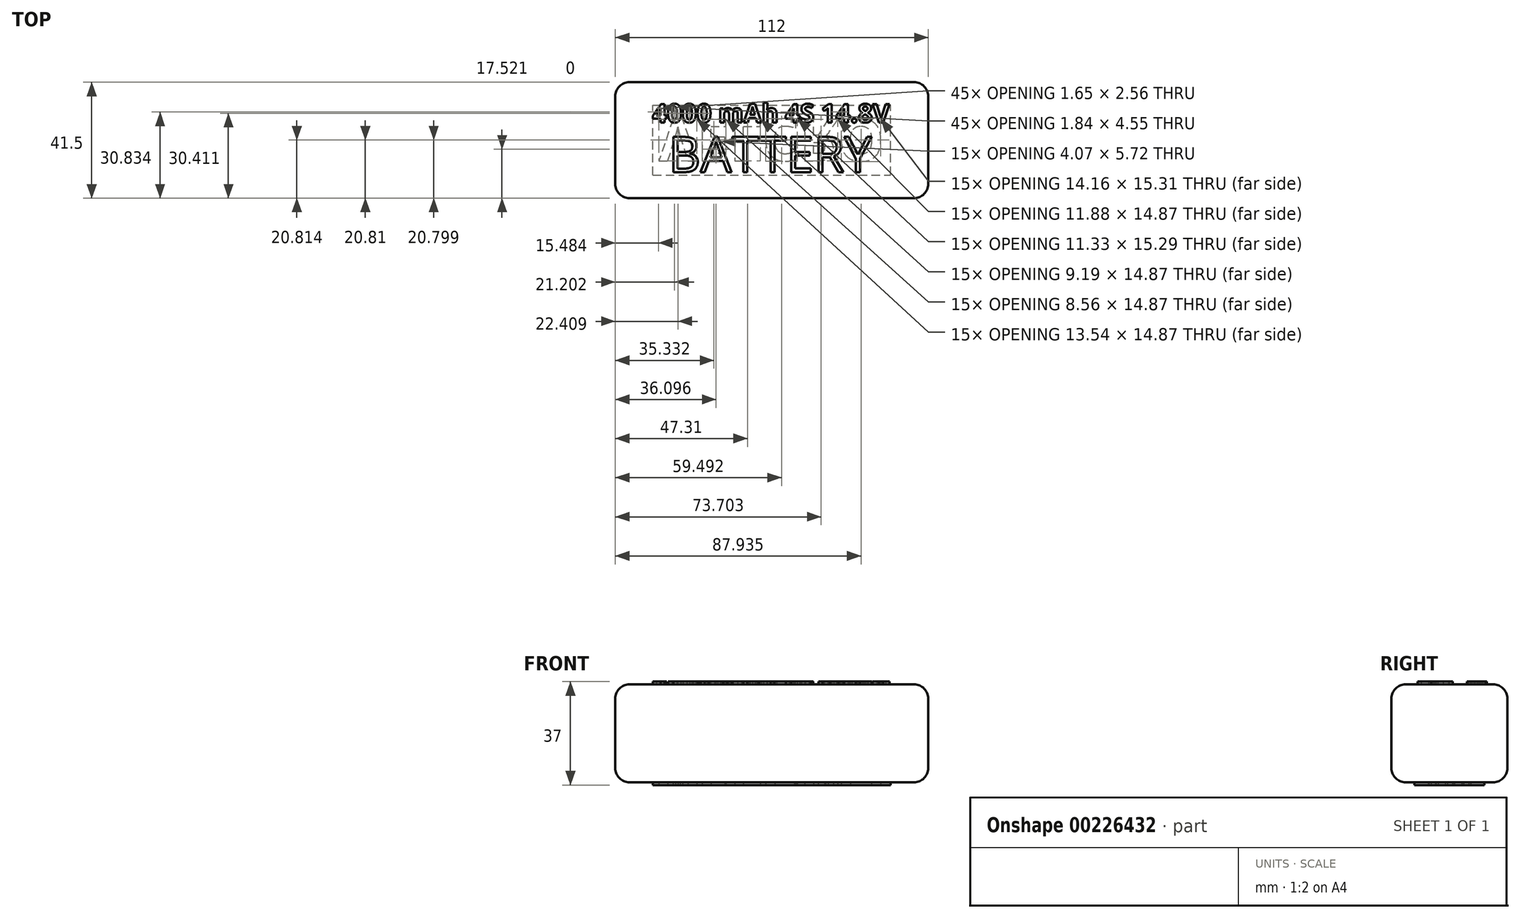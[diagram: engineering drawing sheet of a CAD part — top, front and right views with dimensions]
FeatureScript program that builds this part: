
annotation { "Feature Type Name" : "Feature", "Feature Type Description" : "" }
export const myFeature = defineFeature(function(context is Context, id is Id, definition is map)
    precondition{}
    {
        {
            var Q0;
            Q0=qCreatedBy(makeId("Front.planeOp"),FACE);
            var sketch = newSketch(context, id + "F0", { "sketchPlane" : qUnion([Q0])});
            skLineSegment(sketch, "E0.bottom", {"start": v(0, 0) * mm, "end": v(112, 0) * mm});
            skLineSegment(sketch, "E0.top", {"start": v(0, -35) * mm, "end": v(112, -35) * mm});
            skLineSegment(sketch, "E0.left", {"start": v(0, 0) * mm, "end": v(0, -35) * mm});
            skLineSegment(sketch, "E0.right", {"start": v(112, 0) * mm, "end": v(112, -35) * mm});
            skSolve(sketch);
        }
        {
            var Q0;
            Q0=makeQuery(id+"F0.imprint","IMPRINT",FACE,{"disambiguationData":[TD([[makeQuery(id+"F0.imprint","IMPRINT",EDGE,{"derivedFrom":sQuery(id+"F0.wireOp",EDGE,"E0.bottom")}),-1.0]])]});
            extrude(context, id + "F1", {"entities" : qUnion([Q0]), "depth" : 41.5 * mm, "offsetDistance" : 25.4 * mm});
        }
        {
            var Q0;
            Q0=makeQuery(id+"F1.opExtrude","SWEPT_FACE",FACE,{"disambiguationData":[OSD([sQuery(id+"F0.wireOp",EDGE,"E0.top")])]});
            var sketch = newSketch(context, id + "F2", { "sketchPlane" : qUnion([Q0])});
            skLineSegment(sketch, "E1.bottom", {"start": v(13.5, 33.25) * mm, "end": v(98.5, 33.25) * mm});
            skLineSegment(sketch, "E1.top", {"start": v(13.5, 8.25) * mm, "end": v(98.5, 8.25) * mm});
            skLineSegment(sketch, "E1.left", {"start": v(13.5, 33.25) * mm, "end": v(13.5, 8.25) * mm});
            skLineSegment(sketch, "E1.right", {"start": v(98.5, 33.25) * mm, "end": v(98.5, 8.25) * mm});
            skLineSegment(sketch, "E2", {"start": v(43.64, 33.25) * mm, "end": v(43.64, 41.5) * mm});
            skLineSegment(sketch, "E3", {"start": v(98.5, 17.56) * mm, "end": v(112, 17.56) * mm});
            skLineSegment(sketch, "E4", {"start": v(68.94, 8.25) * mm, "end": v(68.94, 0) * mm});
            skLineSegment(sketch, "E5", {"start": v(13.5, 17.8) * mm, "end": v(0, 17.8) * mm});
            skSolve(sketch);
        }
        {
            var Q0;
            {var subQ4=sQuery(id+"F2.wireOp",EDGE,"E1.left");var subQ6=sQuery(id+"F2.wireOp",EDGE,"E1.bottom");var subQ9=makeQuery(id+"F2.imprint","INTERSECT",VERTEX,{"derivedFrom":[subQ6,subQ4]});Q0=makeQuery(id+"F2.imprint","IMPRINT",FACE,{"disambiguationData":[TD([[makeQuery(id+"F2.imprint","IMPRINT",EDGE,{"disambiguationData":[TD([[subQ9,-1.0]])],"derivedFrom":subQ6}),-1.0]])]});}
            extrude(context, id + "F3", {"entities" : qUnion([Q0]), "depth" : 1 * mm, "offsetDistance" : 25.4 * mm});
        }
        {
            var Q0;
            Q0=makeQuery(id+"F1.opExtrude","SWEPT_FACE",FACE,{"disambiguationData":[OSD([sQuery(id+"F0.wireOp",EDGE,"E0.bottom")])]});
            var Q1;
            Q1=makeQuery(id+"F1.opExtrude","SWEPT_FACE",FACE,{"disambiguationData":[OSD([sQuery(id+"F0.wireOp",EDGE,"E0.right")])]});
            var Q2;
            Q2=makeQuery(id+"F1.opExtrude","CAP_FACE",FACE,{"disambiguationData":[OSD([sQuery(id+"F0.wireOp",EDGE,"E0.bottom"),sQuery(id+"F0.wireOp",EDGE,"E0.top"),sQuery(id+"F0.wireOp",EDGE,"E0.left"),sQuery(id+"F0.wireOp",EDGE,"E0.right")])],"isStart":false});
            var Q3;
            Q3=makeQuery(id+"F1.opExtrude","CAP_FACE",FACE,{"disambiguationData":[OSD([sQuery(id+"F0.wireOp",EDGE,"E0.bottom"),sQuery(id+"F0.wireOp",EDGE,"E0.top"),sQuery(id+"F0.wireOp",EDGE,"E0.left"),sQuery(id+"F0.wireOp",EDGE,"E0.right")])],"isStart":true});
            var Q4;
            Q4=makeQuery(id+"F1.opExtrude","SWEPT_FACE",FACE,{"disambiguationData":[OSD([sQuery(id+"F0.wireOp",EDGE,"E0.left")])]});
            fillet(context, id + "F4", {"entities" : qUnion([Q0, Q1, Q2, Q3, Q4]), "radius" : 5.08 * mm, "tangentPropagation" : true, "allowEdgeOverflow" : false});
        }
        {
            var Q0;
            Q0=makeQuery(id+"F1.opExtrude","SWEPT_FACE",FACE,{"disambiguationData":[OSD([sQuery(id+"F0.wireOp",EDGE,"E0.bottom")])]});
            var sketch = newSketch(context, id + "F5", { "sketchPlane" : qUnion([Q0])});
            skText(sketch, "E6", { "text": "4000 mAh 4S 14.8V", "fontName": "OpenSans-Bold.ttf"});
            skLineSegment(sketch, "E7", {"start": v(5.08, -10.72) * mm, "end": v(13.27, -10.72) * mm});
            skLineSegment(sketch, "E8", {"start": v(98.73, -11.07) * mm, "end": v(106.92, -11.07) * mm});
            skText(sketch, "E9", { "text": "BATTERY", "fontName": "OpenSans-Regular.ttf"});
            skLineSegment(sketch, "E10", {"start": v(19.08, -25.81) * mm, "end": v(5.08, -25.81) * mm});
            skLineSegment(sketch, "E11", {"start": v(92.92, -25.81) * mm, "end": v(106.92, -25.81) * mm});
            const initialGuessF5  = {"E6": [0.01327, -0.0144, 1, 0, 0.00667], "E9": [0.01908, -0.03216, 1, 0, 0.0127]};
            skSetInitialGuess(sketch, initialGuessF5);
            skSolve(sketch);
        }
        {
            var Q0;
            Q0 = qSketchRegion(id + "F5", true);
            extrude(context, id + "F6", {"entities" : qUnion([Q0]), "depth" : 1 * mm, "offsetDistance" : 25.4 * mm});
        }
        {
            var Q0;
            Q0=makeQuery(id+"F3.opExtrude","CAP_FACE",FACE,{"disambiguationData":[OSD([sQuery(id+"F2.wireOp",EDGE,"E1.bottom"),sQuery(id+"F2.wireOp",EDGE,"E1.top"),sQuery(id+"F2.wireOp",EDGE,"E1.left"),sQuery(id+"F2.wireOp",EDGE,"E1.right")])],"isStart":false});
            var sketch = newSketch(context, id + "F7", { "sketchPlane" : qUnion([Q0])});
            skText(sketch, "E12", { "text": "VELCRO", "fontName": "OpenSans-Bold.ttf"});
            skLineSegment(sketch, "E13", {"start": v(56, 28.25) * mm, "end": v(56, 33.25) * mm});
            skLineSegment(sketch, "E14", {"start": v(56, 13.25) * mm, "end": v(56, 8.25) * mm});
            skLineSegment(sketch, "E15", {"start": v(96.36, 20.75) * mm, "end": v(98.5, 20.75) * mm});
            skLineSegment(sketch, "E16", {"start": v(15.64, 20.75) * mm, "end": v(13.5, 20.75) * mm});
            const initialGuessF7  = {"E12": [0.01564, 0.01325, 1, 0, 0.015]};
            skSetInitialGuess(sketch, initialGuessF7);
            skSolve(sketch);
        }
        {
            var Q0;
            Q0 = qSketchRegion(id + "F7", true);
            extrude(context, id + "F8", {"entities" : qUnion([Q0]), "operationType" : NewBodyOperationType.REMOVE, "oppositeDirection" : true, "depth" : 1 * mm, "offsetDistance" : 25.4 * mm});
        }
        {
            var Q0;
            Q0=makeQuery(id+"F1.opExtrude","SWEPT_FACE",FACE,{"disambiguationData":[OSD([sQuery(id+"F0.wireOp",EDGE,"E0.top")])]});
            var sketch = newSketch(context, id + "F9", { "sketchPlane" : qUnion([Q0])});
            skLineSegment(sketch, "E17.0", {"start": v(56, 28.25) * mm, "end": v(56, 33.25) * mm});
            skLineSegment(sketch, "E17.1", {"start": v(56, 13.25) * mm, "end": v(56, 8.25) * mm});
            skLineSegment(sketch, "E17.2", {"start": v(96.36, 20.75) * mm, "end": v(98.5, 20.75) * mm});
            skLineSegment(sketch, "E17.3", {"start": v(15.64, 20.75) * mm, "end": v(13.5, 20.75) * mm});
            skLineSegment(sketch, "E18.0", {"start": v(15.64, 13.25) * mm, "end": v(15.64, 28.25) * mm, "construction": true});
            skLineSegment(sketch, "E19.0", {"start": v(15.64, 13.25) * mm, "end": v(96.36, 13.25) * mm, "construction": true});
            skLineSegment(sketch, "E20.0", {"start": v(15.64, 28.25) * mm, "end": v(96.36, 28.25) * mm, "construction": true});
            skLineSegment(sketch, "E21.0", {"start": v(96.36, 13.25) * mm, "end": v(96.36, 28.25) * mm, "construction": true});
            skLineSegment(sketch, "E22.0.0", {"start": v(98.5, 8.25) * mm, "end": v(98.5, 20.75) * mm});
            skLineSegment(sketch, "E22.0.1", {"start": v(98.5, 20.75) * mm, "end": v(98.5, 33.25) * mm});
            skLineSegment(sketch, "E22.0.2", {"start": v(98.5, 33.25) * mm, "end": v(56, 33.25) * mm});
            skLineSegment(sketch, "E22.0.3", {"start": v(56, 33.25) * mm, "end": v(13.5, 33.25) * mm});
            skLineSegment(sketch, "E22.0.4", {"start": v(13.5, 33.25) * mm, "end": v(13.5, 20.75) * mm});
            skLineSegment(sketch, "E22.0.5", {"start": v(13.5, 20.75) * mm, "end": v(13.5, 8.25) * mm});
            skLineSegment(sketch, "E22.0.6", {"start": v(13.5, 8.25) * mm, "end": v(56, 8.25) * mm});
            skLineSegment(sketch, "E22.0.7", {"start": v(56, 8.25) * mm, "end": v(98.5, 8.25) * mm});
            skText(sketch, "E23", { "text": "VELCRO\n", "fontName": "OpenSans-Bold.ttf"});
            const initialGuessF9  = {"E23": [0.01564, 0.01325, 1, 0, 0.015]};
            skSetInitialGuess(sketch, initialGuessF9);
            skSolve(sketch);
        }
        {
            var Q0;
            Q0=makeQuery(id+"F9.imprint","IMPRINT",FACE,{"disambiguationData":[TD([[makeQuery(id+"F9.imprint","IMPRINT",EDGE,{"derivedFrom":sQuery(id+"F9.wireOp",EDGE,"E23.sketch_text.stroke-0")}),-1.0]])]});
            var Q1;
            Q1=makeQuery(id+"F9.imprint","IMPRINT",FACE,{"disambiguationData":[TD([[makeQuery(id+"F9.imprint","IMPRINT",EDGE,{"derivedFrom":sQuery(id+"F9.wireOp",EDGE,"E23.sketch_text.stroke-10")}),-1.0]])]});
            var Q2;
            Q2=makeQuery(id+"F9.imprint","IMPRINT",FACE,{"disambiguationData":[TD([[makeQuery(id+"F9.imprint","IMPRINT",EDGE,{"derivedFrom":sQuery(id+"F9.wireOp",EDGE,"E23.sketch_text.stroke-22")}),-1.0]])]});
            var Q3;
            Q3=makeQuery(id+"F9.imprint","IMPRINT",FACE,{"disambiguationData":[TD([[makeQuery(id+"F9.imprint","IMPRINT",EDGE,{"derivedFrom":sQuery(id+"F9.wireOp",EDGE,"E23.sketch_text.stroke-28")}),-1.0]])]});
            var Q4;
            Q4=makeQuery(id+"F9.imprint","IMPRINT",FACE,{"disambiguationData":[TD([[makeQuery(id+"F9.imprint","IMPRINT",EDGE,{"derivedFrom":sQuery(id+"F9.wireOp",EDGE,"E23.sketch_text.stroke-43")}),-1.0]])]});
            var Q5;
            Q5=makeQuery(id+"F9.imprint","IMPRINT",FACE,{"disambiguationData":[TD([[makeQuery(id+"F9.imprint","IMPRINT",EDGE,{"derivedFrom":sQuery(id+"F9.wireOp",EDGE,"E23.sketch_text.stroke-62")}),-1.0]])]});
            extrude(context, id + "F10", {"entities" : qUnion([Q0, Q1, Q2, Q3, Q4, Q5]), "depth" : 1 * mm, "offsetDistance" : 25.4 * mm});
        }
    });
